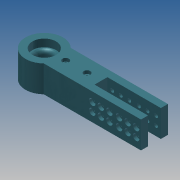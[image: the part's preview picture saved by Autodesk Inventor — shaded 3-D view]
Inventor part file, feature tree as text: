
AUTODESK INVENTOR PART (.ipt)
format: ipt  version: 2013 (Build 170138000, 138)  size: 298,496 bytes
history: native  units: mm
features: extrude x10, sketch x10, pattern_linear x2, fillet x1
ambient origin geometry x8: Origin, YZ Plane, XZ Plane, XY Plane, X Axis, Y Axis, Z Axis, Center Point
bodies: Solid1 (feature_tree)
feature tree (23):
  extrude  "Extrusion1"  Depth=12.6mm
  extrude  "Extrusion2"  Depth=8.5mm
  extrude  "Extrusion3"  Depth=22.0mm
  extrude  "Extrusion4"  Depth=20.0mm
  extrude  "Extrusion5"  Depth=7.0mm TaperAngle=0.0deg
  extrude  "Extrusion6"  Depth=3.5mm
  fillet  "Fillet1"  Radius=35.0mm
  extrude  "Extrusion7"  Depth=6.0mm
  extrude  "Extrusion8"  Depth=8.0mm TaperAngle=0.0deg
  extrude  "Extrusion9"  Depth=12.0mm
  extrude  "Extrusion10"  Depth=50.0mm
  pattern_linear  "Rectangular Pattern1"  Spacing1=10.0mm  [1 undecoded]
  pattern_linear  "Rectangular Pattern2"  Spacing1=12.5mm  [1 undecoded]
  sketch  "Sketch1"  dims[d0=153.0mm d2=12.6mm]
  sketch  "Sketch2"  dims[d3=15.0mm d4=8.5mm]
  sketch  "Sketch4"  dims[d5=25.0mm d6=0.0mm d7=22.0mm]
  sketch  "Sketch5"  dims[d9=7.0mm d10=0.0mm d16=20.0mm]
  sketch  "Sketch6"  dims[d17=40.0mm d18=7.0mm d19=0.0mm]
  sketch  "Sketch7"  dims[d21=3.0mm d22=0.0mm d23=3.5mm d24=35.0mm]
  sketch  "Sketch8"  dims[d26=10.0mm d27=0.0mm d28=6.0mm]
  sketch  "Sketch9"  dims[d30=14.0mm d32=8.0mm d33=0.0mm]
  sketch  "Sketch10"  dims[d34=3.5mm d35=12.0mm]
  sketch  "Sketch11"  dims[d37=50.0mm d38=50.0mm d39=10.0mm d40=0.0mm d41=12.5mm d42=8.0mm d43=3.5mm d44=10.0mm d45=0.0mm d46=6.0mm d48=3.0mm d49=0.0mm d50=5.5mm d51=4.0mm d52=0.0mm d53=30.0mm d55=8.0mm d56=20.0mm d58=8.0mm d59=20.0mm d61=25.0mm]
note: 2 required parameter values undecoded (feature->parameter linkage not recoverable at this tier; creation-order binding heuristic only, values carry confidence <= 0.55)
